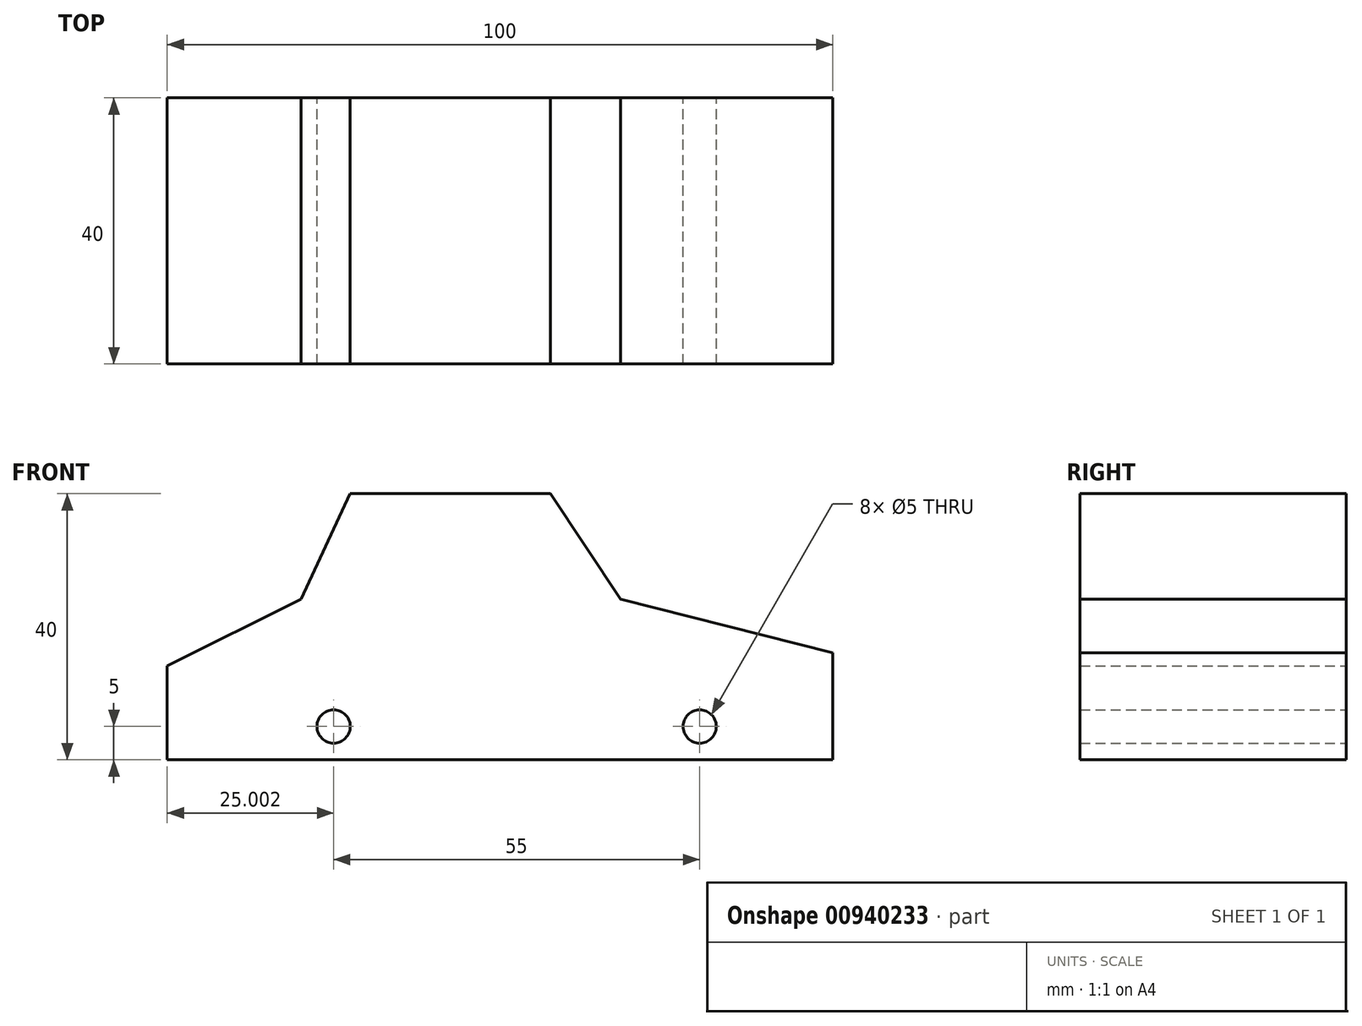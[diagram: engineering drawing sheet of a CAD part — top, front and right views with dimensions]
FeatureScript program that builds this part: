
annotation { "Feature Type Name" : "Feature", "Feature Type Description" : "" }
export const myFeature = defineFeature(function(context is Context, id is Id, definition is map)
    precondition{}
    {
        {
            var Q0;
            Q0=qCreatedBy(makeId("Front.planeOp"),FACE);
            var sketch = newSketch(context, id + "F0", { "sketchPlane" : qUnion([Q0])});
            skLineSegment(sketch, "E0", {"start": v(-49.92, 0) * mm, "end": v(50.08, 0) * mm, "construction": true});
            skLineSegment(sketch, "E1", {"start": v(-49.92, 5) * mm, "end": v(50.08, 5) * mm, "construction": true});
            skLineSegment(sketch, "E2", {"start": v(-49.92, 40) * mm, "end": v(50.08, 40) * mm, "construction": true});
            skLineSegment(sketch, "E3", {"start": v(-49.92, 0) * mm, "end": v(-49.92, 40) * mm, "construction": true});
            skLineSegment(sketch, "E4", {"start": v(50.08, 0) * mm, "end": v(50.08, 40) * mm, "construction": true});
            skLineSegment(sketch, "E5", {"start": v(-24.92, 30.62) * mm, "end": v(-24.92, -18.3) * mm, "construction": true});
            skLineSegment(sketch, "E6", {"start": v(30.08, 29.86) * mm, "end": v(30.08, -19.24) * mm, "construction": true});
            skCircle(sketch, "E7", {"center": v(-24.92, 5) * mm, "radius": 12.5 * mm, "construction": true});
            skCircle(sketch, "E8", {"center": v(30.08, 5) * mm, "radius": 12.5 * mm, "construction": true});
            skCircle(sketch, "E9", {"center": v(-24.92, 5) * mm, "radius": 2.5 * mm});
            skCircle(sketch, "E10", {"center": v(30.08, 5) * mm, "radius": 2.5 * mm});
            skLineSegment(sketch, "E11", {"start": v(-49.92, 0) * mm, "end": v(50.08, 0) * mm});
            skLineSegment(sketch, "E12", {"start": v(50.08, 16.05) * mm, "end": v(18.2, 24.17) * mm});
            skLineSegment(sketch, "E13", {"start": v(18.2, 24.17) * mm, "end": v(7.68, 40) * mm});
            skLineSegment(sketch, "E14", {"start": v(7.68, 40) * mm, "end": v(-22.47, 40) * mm});
            skLineSegment(sketch, "E15", {"start": v(-22.47, 40) * mm, "end": v(-29.8, 24.17) * mm});
            skLineSegment(sketch, "E16", {"start": v(-29.8, 24.17) * mm, "end": v(-49.92, 14.09) * mm});
            skLineSegment(sketch, "E17", {"start": v(-49.92, 14.09) * mm, "end": v(-49.92, 0) * mm});
            skLineSegment(sketch, "E18", {"start": v(50.08, 0) * mm, "end": v(50.08, 16.05) * mm});
            skSolve(sketch);
        }
        {
            var Q0;
            Q0=makeQuery(id+"F0.imprint","IMPRINT",FACE,{"disambiguationData":[TD([[makeQuery(id+"F0.imprint","IMPRINT",EDGE,{"derivedFrom":sQuery(id+"F0.wireOp",EDGE,"E9")}),-1.0]])]});
            extrude(context, id + "F1", {"entities" : qUnion([Q0]), "depth" : 40 * mm, "offsetDistance" : 25 * mm});
        }
    });
